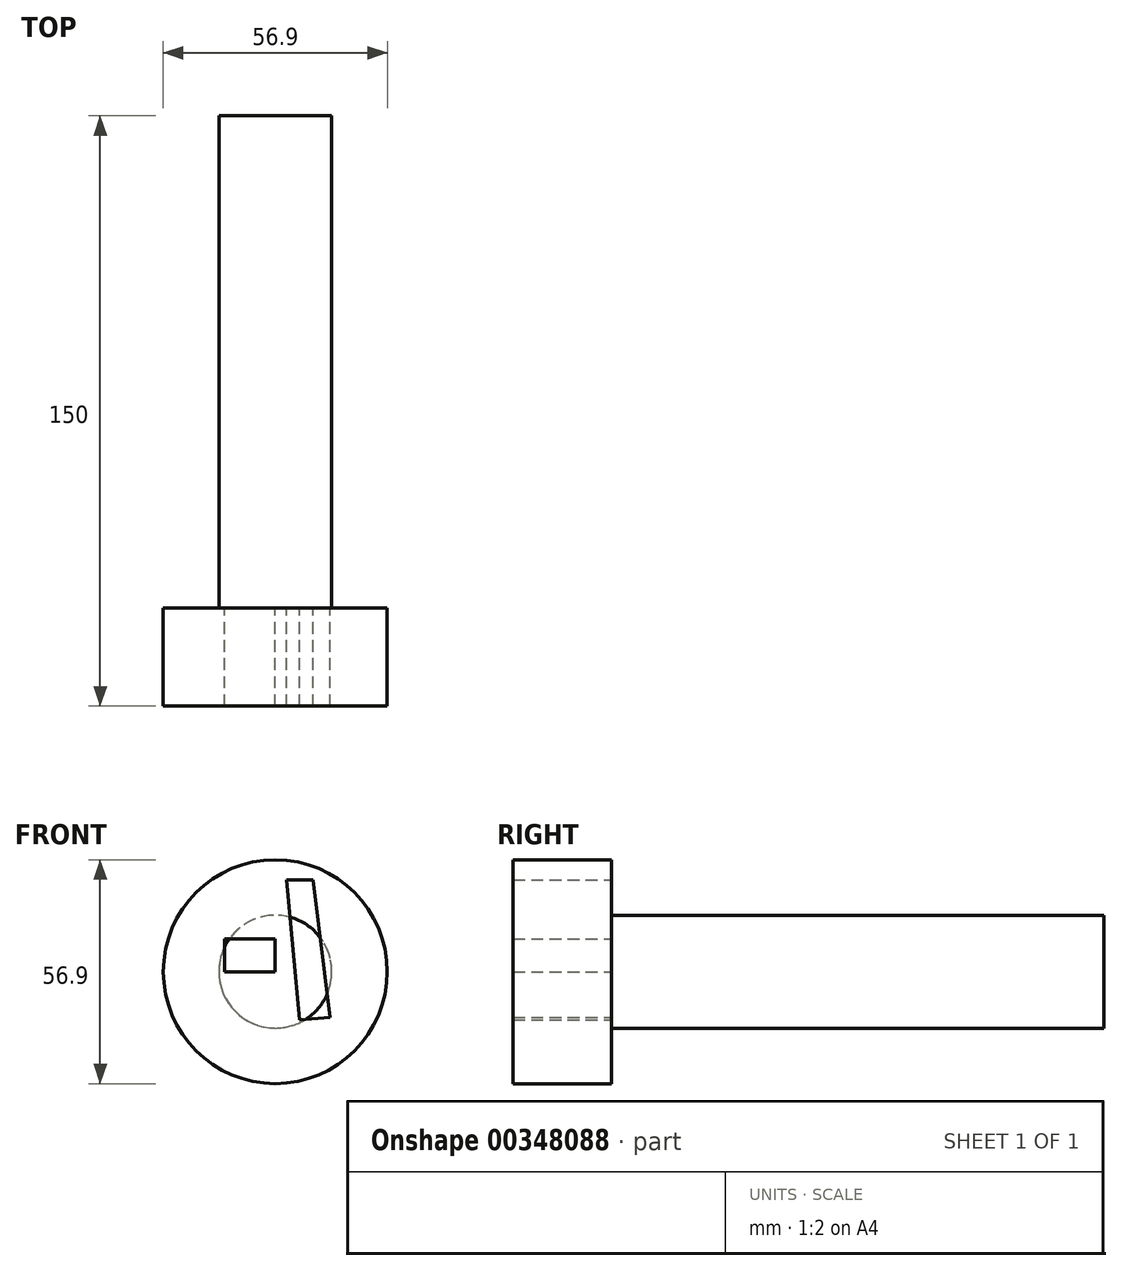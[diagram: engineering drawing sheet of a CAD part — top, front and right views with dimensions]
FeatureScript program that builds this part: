
annotation { "Feature Type Name" : "Feature", "Feature Type Description" : "" }
export const myFeature = defineFeature(function(context is Context, id is Id, definition is map)
    precondition{}
    {
        {
            var Q0;
            Q0=qCreatedBy(makeId("Front.planeOp"),FACE);
            var sketch = newSketch(context, id + "F0", { "sketchPlane" : qUnion([Q0])});
            skCircle(sketch, "E0", {"center": v(0, 0) * mm, "radius": 28.45 * mm});
            skSolve(sketch);
        }
        {
            var Q0;
            Q0 = qSketchRegion(id + "F0", true);
            extrude(context, id + "F1", {"entities" : qUnion([Q0]), "depth" : 25 * mm});
        }
        {
            var Q0;
            Q0=qCreatedBy(makeId("Front.planeOp"),FACE);
            var sketch = newSketch(context, id + "F2", { "sketchPlane" : qUnion([Q0])});
            skLineSegment(sketch, "E1.bottom", {"start": v(0, 0) * mm, "end": v(-12.86, 0) * mm});
            skLineSegment(sketch, "E1.top", {"start": v(0, 8.37) * mm, "end": v(-12.86, 8.37) * mm});
            skLineSegment(sketch, "E1.left", {"start": v(0, 0) * mm, "end": v(0, 8.37) * mm});
            skLineSegment(sketch, "E1.right", {"start": v(-12.86, 0) * mm, "end": v(-12.86, 8.37) * mm});
            skSolve(sketch);
        }
        {
            var Q0;
            Q0 = qSketchRegion(id + "F2", true);
            extrude(context, id + "F3", {"entities" : qUnion([Q0]), "operationType" : NewBodyOperationType.REMOVE, "depth" : 25 * mm});
        }
        {
            var Q0;
            Q0=qCreatedBy(makeId("Front.planeOp"),FACE);
            var sketch = newSketch(context, id + "F4", { "sketchPlane" : qUnion([Q0])});
            skLineSegment(sketch, "E2", {"start": v(9.61, 23.33) * mm, "end": v(2.88, 23.33) * mm});
            skLineSegment(sketch, "E3", {"start": v(2.88, 23.33) * mm, "end": v(6.16, -12.26) * mm});
            skLineSegment(sketch, "E4", {"start": v(6.16, -12.26) * mm, "end": v(13.9, -11.55) * mm});
            skLineSegment(sketch, "E5", {"start": v(13.9, -11.55) * mm, "end": v(9.61, 23.33) * mm});
            skSolve(sketch);
        }
        {
            var Q0;
            Q0 = qSketchRegion(id + "F4", true);
            extrude(context, id + "F5", {"entities" : qUnion([Q0]), "operationType" : NewBodyOperationType.REMOVE, "depth" : 25 * mm});
        }
        {
            var Q0;
            Q0=qCreatedBy(makeId("Front.planeOp"),FACE);
            var sketch = newSketch(context, id + "F6", { "sketchPlane" : qUnion([Q0])});
            skCircle(sketch, "E6", {"center": v(0, 0) * mm, "radius": 14.34 * mm});
            skSolve(sketch);
        }
        {
            var Q0;
            Q0 = qSketchRegion(id + "F6", true);
            extrude(context, id + "F7", {"entities" : qUnion([Q0]), "operationType" : NewBodyOperationType.ADD, "oppositeDirection" : true, "depth" : 125 * mm});
        }
    });
